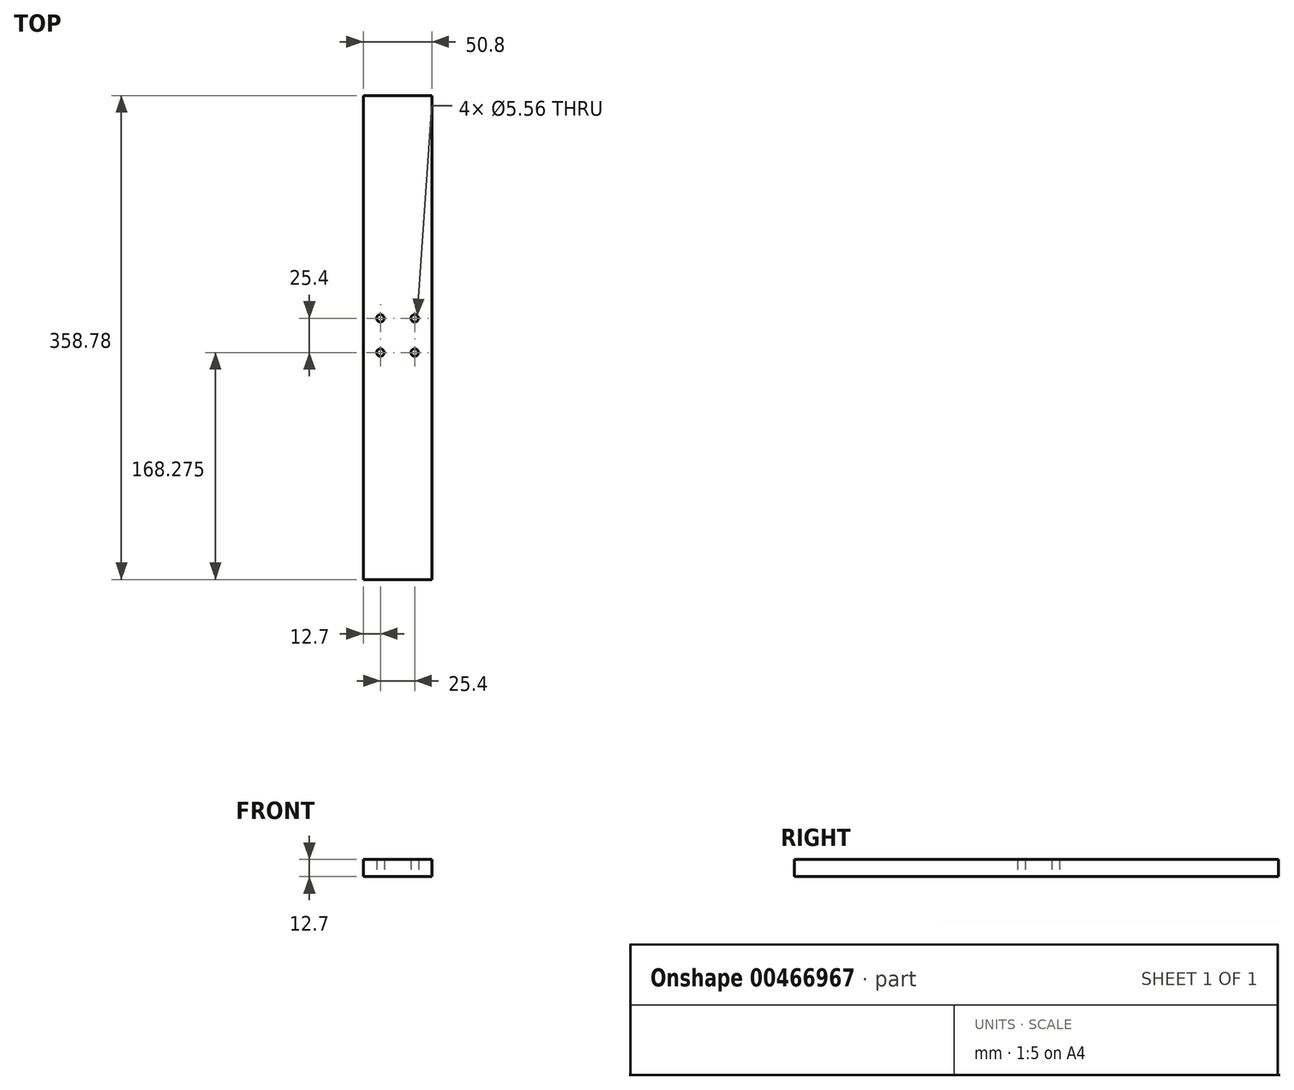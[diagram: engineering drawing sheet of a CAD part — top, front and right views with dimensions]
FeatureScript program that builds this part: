
annotation { "Feature Type Name" : "Feature", "Feature Type Description" : "" }
export const myFeature = defineFeature(function(context is Context, id is Id, definition is map)
    precondition{}
    {
        {
            var Q0;
            Q0=qCreatedBy(makeId("Top.planeOp"),FACE);
            var sketch = newSketch(context, id + "F0", { "sketchPlane" : qUnion([Q0])});
            skLineSegment(sketch, "E0.bottom", {"start": v(0, 0) * mm, "end": v(50.8, 0) * mm});
            skLineSegment(sketch, "E0.top", {"start": v(0, 358.78) * mm, "end": v(50.8, 358.78) * mm});
            skLineSegment(sketch, "E0.left", {"start": v(0, 0) * mm, "end": v(0, 358.78) * mm});
            skLineSegment(sketch, "E0.right", {"start": v(50.8, 0) * mm, "end": v(50.8, 358.78) * mm});
            skCircle(sketch, "E1", {"center": v(12.7, 193.67) * mm, "radius": 2.78 * mm});
            skCircle(sketch, "E2", {"center": v(38.1, 193.67) * mm, "radius": 2.78 * mm});
            skCircle(sketch, "E3", {"center": v(12.7, 168.27) * mm, "radius": 2.78 * mm});
            skCircle(sketch, "E4", {"center": v(38.1, 168.27) * mm, "radius": 2.78 * mm});
            skSolve(sketch);
        }
        {
            var Q0;
            Q0=makeQuery(id+"F0.imprint","IMPRINT",FACE,{"disambiguationData":[TD([[makeQuery(id+"F0.imprint","IMPRINT",EDGE,{"derivedFrom":sQuery(id+"F0.wireOp",EDGE,"E0.bottom")}),1.0]])]});
            extrude(context, id + "F1", {"entities" : qUnion([Q0]), "depth" : 12.7 * mm});
        }
    });
